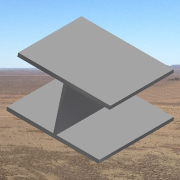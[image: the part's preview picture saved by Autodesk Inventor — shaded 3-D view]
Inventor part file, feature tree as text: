
AUTODESK INVENTOR PART (.ipt)
format: ipt  version: 2014 SP1 (Build 180222100, 222)  size: 128,000 bytes
history: native  units: in
note: dims shown in document units (in); Inventor stores cm internally (conversion verified against a paired STEP export)
features: other x3, sketch x2
ambient origin geometry x8: Origin, YZ Plane, XZ Plane, XY Plane, X Axis, Y Axis, Z Axis, Center Point
bodies: Solid1 (feature_tree)
feature tree (5):
  other  "endVert1.ipt"
  other  "Solid2::endVert1.ipt"
  other  "TaggingFeature1"
  sketch  "Sketch1"  dims[d0=0.3937in]
  sketch  "Sketch6"  dims[d2=0.12in d17=0.12in d18=3.0in d19=0.0in d20=15.0deg d21=-0.5in d22=1.0in d23=0.0in]
